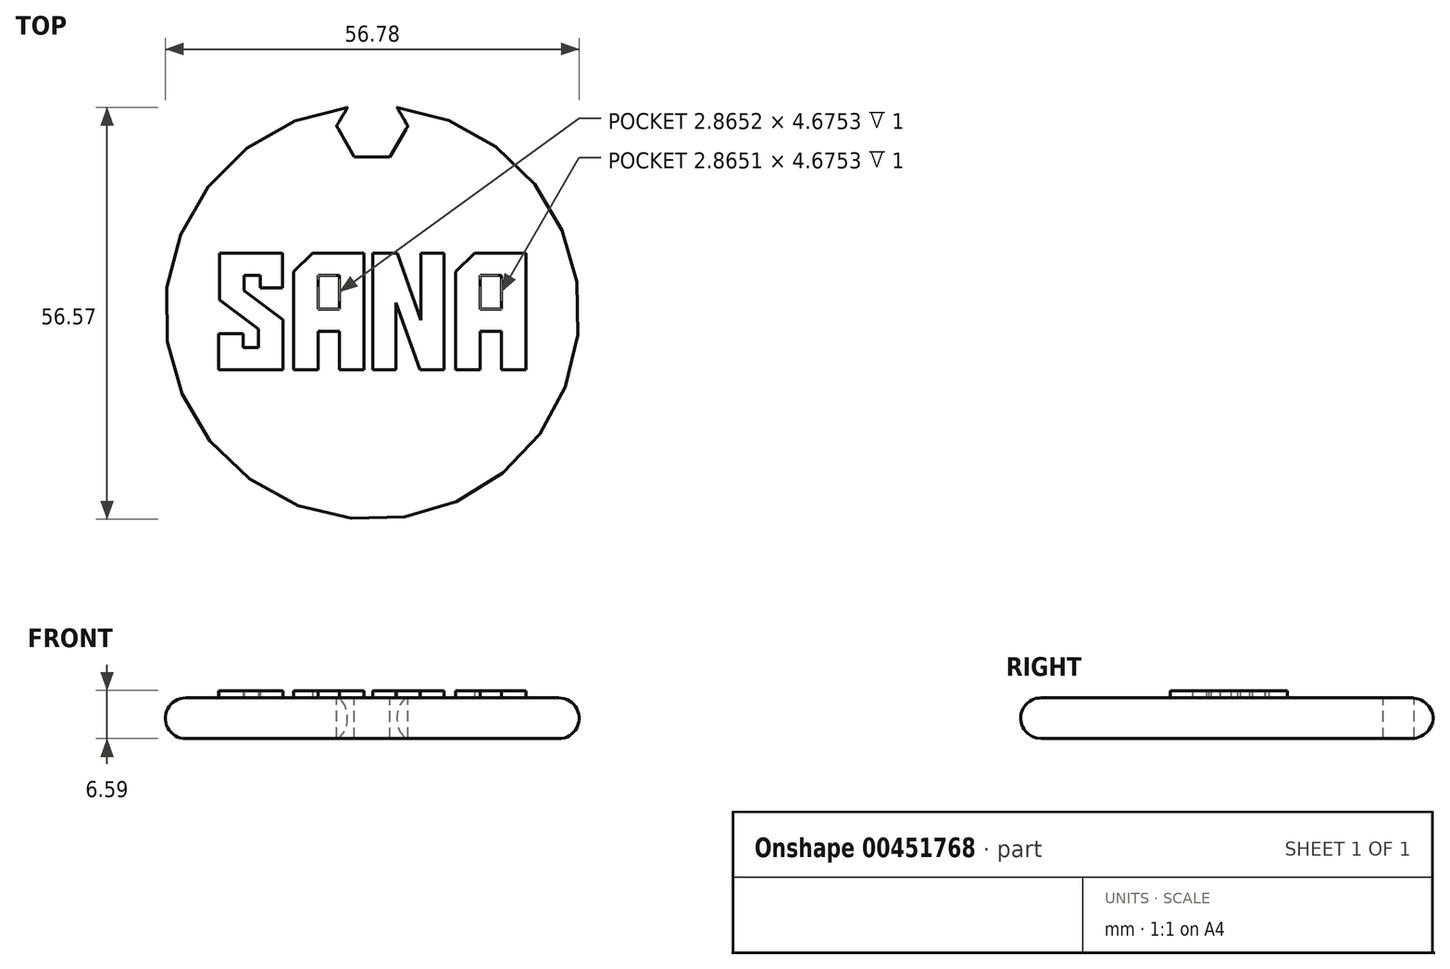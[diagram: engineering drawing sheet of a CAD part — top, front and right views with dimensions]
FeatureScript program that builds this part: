
annotation { "Feature Type Name" : "Feature", "Feature Type Description" : "" }
export const myFeature = defineFeature(function(context is Context, id is Id, definition is map)
    precondition{}
    {
        {
            var Q0;
            Q0=qCreatedBy(makeId("Front.planeOp"),FACE);
            var sketch = newSketch(context, id + "F0", { "sketchPlane" : qUnion([Q0])});
            skLineSegment(sketch, "E0.bottom", {"start": v(0, 0) * mm, "end": v(-25.6, 0) * mm});
            skLineSegment(sketch, "E0.top", {"start": v(0, 5.59) * mm, "end": v(-25.6, 5.59) * mm});
            skLineSegment(sketch, "E0.left", {"start": v(0, 0) * mm, "end": v(0, 5.59) * mm});
            skLineSegment(sketch, "E0.right", {"start": v(-25.6, 0) * mm, "end": v(-25.6, 5.59) * mm});
            skArc(sketch, "E1", {"start": v(-25.6, 5.59) * mm, "mid": v(-28.39, 2.8) * mm, "end": v(-25.6, 0) * mm});
            skSolve(sketch);
        }
        {
            var Q0;
            Q0 = qSketchRegion(id + "F0", true);
            var Q1;
            Q1=sQuery(id+"F0.wireOp",EDGE,"E0.left");
            revolve(context, id + "F1", {"entities" : qUnion([Q0]), "axis" : qUnion([Q1]), "revolveType" : RevolveType.FULL});
        }
        {
            var Q0;
            Q0=makeQuery(id+"F1.opRevolve","SWEPT_FACE",FACE,{"disambiguationData":[OSD([sQuery(id+"F0.wireOp",EDGE,"E0.top")])]});
            var sketch = newSketch(context, id + "F2", { "sketchPlane" : qUnion([Q0])});
            skLineSegment(sketch, "E2", {"start": v(-21.06, -7.88) * mm, "end": v(-21.06, -2.88) * mm});
            skLineSegment(sketch, "E3", {"start": v(-21.06, -2.88) * mm, "end": v(-17.7, -2.88) * mm});
            skLineSegment(sketch, "E4", {"start": v(-17.7, -2.88) * mm, "end": v(-17.7, -4.84) * mm});
            skLineSegment(sketch, "E5", {"start": v(-17.7, -4.84) * mm, "end": v(-15.6, -4.84) * mm});
            skLineSegment(sketch, "E6", {"start": v(-15.6, -4.84) * mm, "end": v(-15.6, -2.28) * mm});
            skLineSegment(sketch, "E7", {"start": v(-15.6, -2.28) * mm, "end": v(-20.94, 1.75) * mm});
            skLineSegment(sketch, "E8", {"start": v(-20.94, 1.75) * mm, "end": v(-20.94, 8.18) * mm});
            skLineSegment(sketch, "E9", {"start": v(-20.94, 8.18) * mm, "end": v(-12.33, 8.18) * mm});
            skLineSegment(sketch, "E10", {"start": v(-12.33, 8.18) * mm, "end": v(-12.33, 3.4) * mm});
            skLineSegment(sketch, "E11", {"start": v(-12.33, 3.4) * mm, "end": v(-15.38, 3.4) * mm});
            skLineSegment(sketch, "E12", {"start": v(-15.38, 3.4) * mm, "end": v(-15.38, 5.11) * mm});
            skLineSegment(sketch, "E13", {"start": v(-15.38, 5.11) * mm, "end": v(-17.58, 5.11) * mm});
            skLineSegment(sketch, "E14", {"start": v(-17.58, 5.11) * mm, "end": v(-17.58, 3.02) * mm});
            skLineSegment(sketch, "E15", {"start": v(-17.58, 3.02) * mm, "end": v(-12.23, -1) * mm});
            skLineSegment(sketch, "E16", {"start": v(-12.23, -1) * mm, "end": v(-12.23, -7.88) * mm});
            skLineSegment(sketch, "E17", {"start": v(-7.4, -7.88) * mm, "end": v(-10.77, -7.88) * mm});
            skLineSegment(sketch, "E18", {"start": v(-10.77, -7.88) * mm, "end": v(-10.77, 5.64) * mm});
            skLineSegment(sketch, "E19", {"start": v(-10.77, 5.64) * mm, "end": v(-8.18, 8.18) * mm});
            skLineSegment(sketch, "E20", {"start": v(-8.18, 8.18) * mm, "end": v(-1.17, 8.18) * mm});
            skLineSegment(sketch, "E21", {"start": v(-1.17, 8.18) * mm, "end": v(-1.17, -7.88) * mm});
            skLineSegment(sketch, "E22", {"start": v(-1.17, -7.88) * mm, "end": v(-4.53, -7.88) * mm});
            skLineSegment(sketch, "E23", {"start": v(-4.53, -7.88) * mm, "end": v(-4.53, -2.6) * mm});
            skLineSegment(sketch, "E24", {"start": v(-4.53, -2.6) * mm, "end": v(-7.4, -2.6) * mm});
            skLineSegment(sketch, "E25", {"start": v(-7.4, -2.6) * mm, "end": v(-7.4, -7.88) * mm});
            skLineSegment(sketch, "E26", {"start": v(-4.53, 0.45) * mm, "end": v(-4.53, 5.13) * mm});
            skLineSegment(sketch, "E27", {"start": v(-4.53, 5.13) * mm, "end": v(-7.4, 5.13) * mm});
            skLineSegment(sketch, "E28", {"start": v(-7.4, 5.13) * mm, "end": v(-7.4, 0.45) * mm});
            skLineSegment(sketch, "E29", {"start": v(-7.4, 0.45) * mm, "end": v(-4.53, 0.45) * mm});
            skLineSegment(sketch, "E30", {"start": v(6.7, -1.04) * mm, "end": v(6.7, 8.18) * mm});
            skLineSegment(sketch, "E31", {"start": v(6.7, 8.18) * mm, "end": v(9.87, 8.18) * mm});
            skLineSegment(sketch, "E32", {"start": v(9.87, 8.18) * mm, "end": v(9.87, -7.88) * mm});
            skLineSegment(sketch, "E33", {"start": v(9.87, -7.88) * mm, "end": v(6.54, -7.88) * mm});
            skLineSegment(sketch, "E34", {"start": v(6.54, -7.88) * mm, "end": v(3.25, 1.34) * mm});
            skLineSegment(sketch, "E35", {"start": v(3.25, 1.34) * mm, "end": v(3.25, -7.88) * mm});
            skLineSegment(sketch, "E36", {"start": v(3.25, -7.88) * mm, "end": v(0.1, -7.88) * mm});
            skLineSegment(sketch, "E37", {"start": v(0.1, -7.88) * mm, "end": v(0.1, 8.18) * mm});
            skLineSegment(sketch, "E38", {"start": v(0.1, 8.18) * mm, "end": v(3.43, 8.18) * mm});
            skLineSegment(sketch, "E39", {"start": v(3.43, 8.18) * mm, "end": v(6.7, -1.04) * mm});
            skLineSegment(sketch, "E40", {"start": v(14.83, -7.88) * mm, "end": v(11.45, -7.88) * mm});
            skLineSegment(sketch, "E41", {"start": v(11.45, -7.88) * mm, "end": v(11.45, 5.64) * mm});
            skLineSegment(sketch, "E42", {"start": v(11.45, 5.64) * mm, "end": v(14.04, 8.18) * mm});
            skLineSegment(sketch, "E43", {"start": v(14.04, 8.18) * mm, "end": v(21.06, 8.18) * mm});
            skLineSegment(sketch, "E44", {"start": v(21.06, 8.18) * mm, "end": v(21.06, -7.88) * mm});
            skLineSegment(sketch, "E45", {"start": v(21.06, -7.88) * mm, "end": v(17.7, -7.88) * mm});
            skLineSegment(sketch, "E46", {"start": v(17.7, -7.88) * mm, "end": v(17.7, -2.6) * mm});
            skLineSegment(sketch, "E47", {"start": v(17.7, -2.6) * mm, "end": v(14.83, -2.6) * mm});
            skLineSegment(sketch, "E48", {"start": v(14.83, -2.6) * mm, "end": v(14.83, -7.88) * mm});
            skLineSegment(sketch, "E49", {"start": v(17.7, 0.45) * mm, "end": v(17.7, 5.13) * mm});
            skLineSegment(sketch, "E50", {"start": v(17.7, 5.13) * mm, "end": v(14.83, 5.13) * mm});
            skLineSegment(sketch, "E51", {"start": v(14.83, 5.13) * mm, "end": v(14.83, 0.45) * mm});
            skLineSegment(sketch, "E52", {"start": v(14.83, 0.45) * mm, "end": v(17.7, 0.45) * mm});
            skLineSegment(sketch, "E53", {"start": v(-21.06, -7.88) * mm, "end": v(-12.23, -7.88) * mm});
            skSolve(sketch);
        }
        {
            var Q0;
            Q0 = qSketchRegion(id + "F2", true);
            extrude(context, id + "F3", {"entities" : qUnion([Q0]), "operationType" : NewBodyOperationType.ADD, "depth" : 1 * mm});
        }
        {
            var Q0;
            Q0=makeQuery(id+"F3.boolean.opBoolean","SPLIT",FACE,{"disambiguationData":[TD([makeQuery(id+"F1.opRevolve","SWEPT_FACE",FACE,{"disambiguationData":[OSD([sQuery(id+"F0.wireOp",EDGE,"E1")])]})])],"derivedFrom":makeQuery(id+"F1.opRevolve","SWEPT_FACE",FACE,{"disambiguationData":[OSD([sQuery(id+"F0.wireOp",EDGE,"E0.top")])]})});
            var sketch = newSketch(context, id + "F4", { "sketchPlane" : qUnion([Q0])});
            skCircle(sketch, "E54.cCircle", {"center": v(0, 25.6) * mm, "radius": 4.23 * mm, "construction": true});
            skLineSegment(sketch, "E54.0", {"start": v(2.44, 21.36) * mm, "end": v(-2.44, 21.36) * mm});
            skLineSegment(sketch, "E54.1", {"start": v(-2.44, 21.36) * mm, "end": v(-4.89, 25.6) * mm});
            skLineSegment(sketch, "E54.2", {"start": v(-4.89, 25.6) * mm, "end": v(-2.44, 29.83) * mm});
            skLineSegment(sketch, "E54.3", {"start": v(-2.44, 29.83) * mm, "end": v(2.44, 29.83) * mm});
            skLineSegment(sketch, "E54.4", {"start": v(2.44, 29.83) * mm, "end": v(4.89, 25.6) * mm});
            skLineSegment(sketch, "E54.5", {"start": v(4.89, 25.6) * mm, "end": v(2.44, 21.36) * mm});
            skPoint(sketch, "E54.0.midPoint", {"position": v(0, 21.36) * mm});
            skSolve(sketch);
        }
        {
            var Q0;
            Q0 = qSketchRegion(id + "F4", true);
            extrude(context, id + "F5", {"entities" : qUnion([Q0]), "operationType" : NewBodyOperationType.REMOVE, "oppositeDirection" : true, "depth" : 25.4 * mm});
        }
    });
